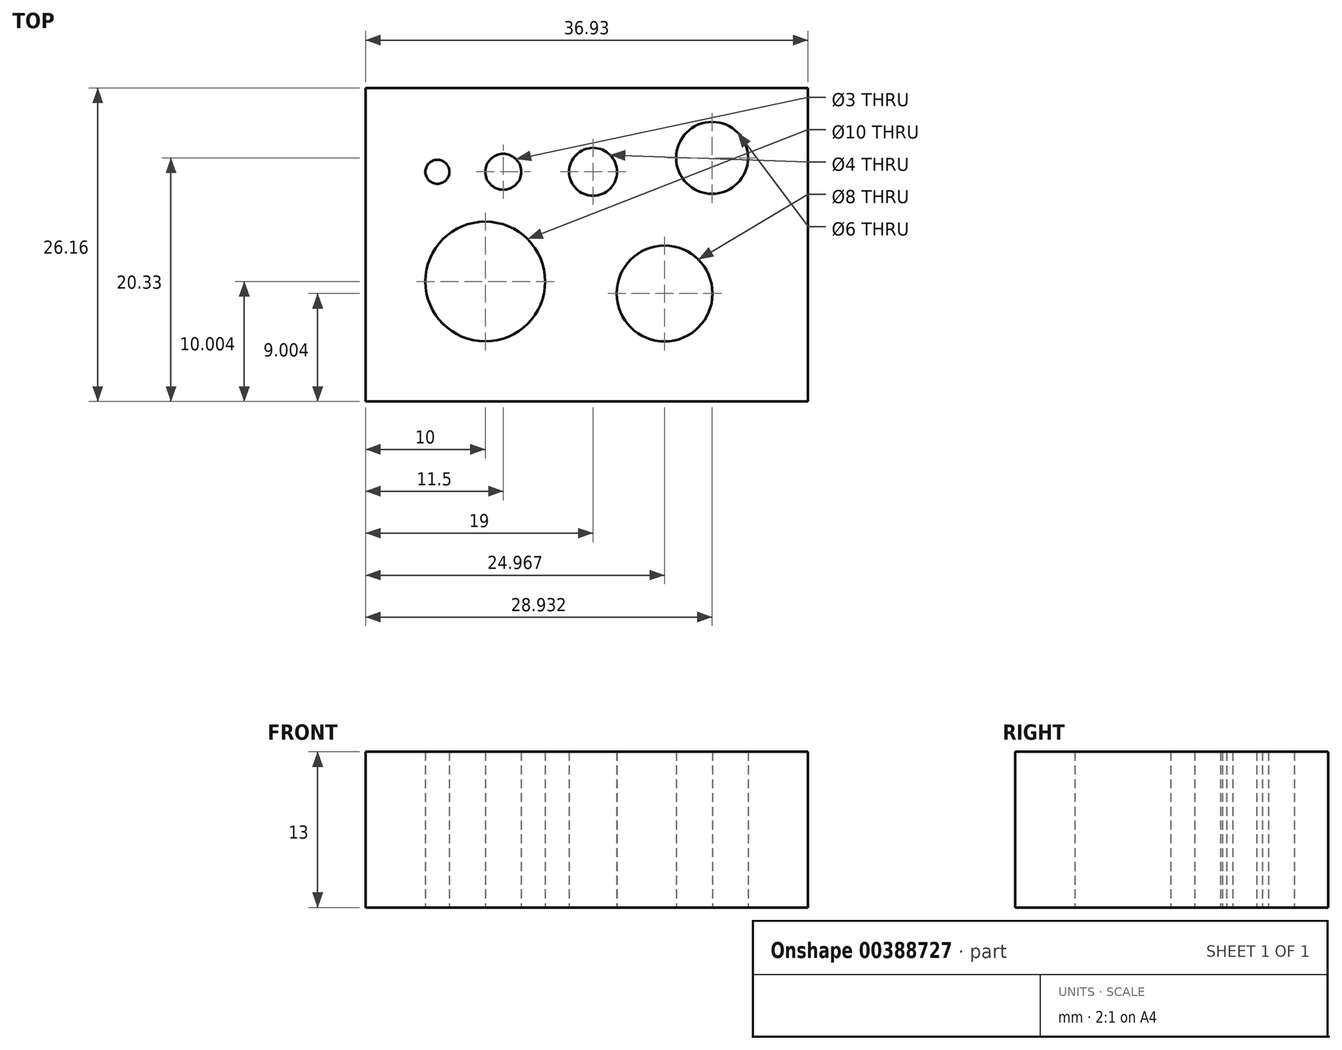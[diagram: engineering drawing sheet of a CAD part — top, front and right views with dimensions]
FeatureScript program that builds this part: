
annotation { "Feature Type Name" : "Feature", "Feature Type Description" : "" }
export const myFeature = defineFeature(function(context is Context, id is Id, definition is map)
    precondition{}
    {
        {
            var Q0;
            Q0=qCreatedBy(makeId("Top.planeOp"),FACE);
            var sketch = newSketch(context, id + "F0", { "sketchPlane" : qUnion([Q0])});
            skLineSegment(sketch, "E0.bottom", {"start": v(-14, 9.57) * mm, "end": v(22.93, 9.57) * mm});
            skLineSegment(sketch, "E0.top", {"start": v(-14, -16.59) * mm, "end": v(22.93, -16.59) * mm});
            skLineSegment(sketch, "E0.left", {"start": v(-14, 9.57) * mm, "end": v(-14, -16.59) * mm});
            skLineSegment(sketch, "E0.right", {"start": v(22.93, 9.57) * mm, "end": v(22.93, -16.59) * mm});
            skPoint(sketch, "E0.middle", {"position": v(0, 0) * mm});
            skCircle(sketch, "E1", {"center": v(-8, 2.57) * mm, "radius": 1 * mm});
            skCircle(sketch, "E2", {"center": v(-2.5, 2.57) * mm, "radius": 1.5 * mm});
            skCircle(sketch, "E3", {"center": v(-4, -6.59) * mm, "radius": 5 * mm});
            skCircle(sketch, "E4", {"center": v(5, 2.57) * mm, "radius": 2 * mm});
            skCircle(sketch, "E5", {"center": v(10.97, -7.59) * mm, "radius": 4 * mm});
            skPoint(sketch, "E6", {"position": v(-8, 0) * mm});
            skCircle(sketch, "E7", {"center": v(14.93, 3.74) * mm, "radius": 3 * mm});
            skSolve(sketch);
        }
        {
            var Q0;
            Q0=makeQuery(id+"F0.imprint","IMPRINT",FACE,{"disambiguationData":[TD([[makeQuery(id+"F0.imprint","IMPRINT",EDGE,{"derivedFrom":sQuery(id+"F0.wireOp",EDGE,"E0.bottom")}),-1.0]])]});
            extrude(context, id + "F1", {"entities" : qUnion([Q0]), "depth" : 13 * mm});
        }
    });
